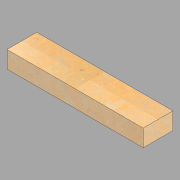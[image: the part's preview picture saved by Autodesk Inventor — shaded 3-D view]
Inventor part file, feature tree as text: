
AUTODESK INVENTOR PART (.ipt)
format: ipt  version: 2022.1 (Build 261234020, 234B)  size: 108,032 bytes
history: native  units: in
note: dims shown in document units (in); Inventor stores cm internally (conversion verified against a paired STEP export)
features: extrude x1, sketch x1
ambient origin geometry x8: Origin, YZ Plane, XZ Plane, XY Plane, X Axis, Y Axis, Z Axis, Center Point
bodies: Solid1 (feature_tree)
feature tree (2):
  extrude  "Extrusion1"  Depth=5.25in
  sketch  "Sketch1"  dims[d0=24.0in d1=5.25in d2=3.0in d3=0.0in]
